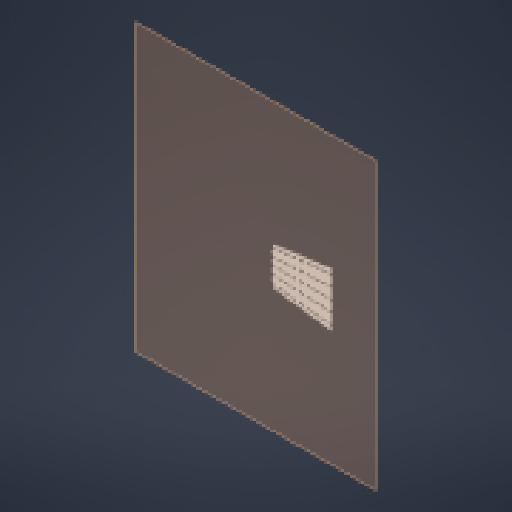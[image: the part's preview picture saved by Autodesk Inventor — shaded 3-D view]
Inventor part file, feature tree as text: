
AUTODESK INVENTOR PART (.ipt)
format: ipt  version: 2023 (Build 270158000, 158)  size: 699,904 bytes
history: native  units: in
note: dims shown in document units (in); Inventor stores cm internally (conversion verified against a paired STEP export)
features: extrude x3, sketch x3, plane x1
ambient origin geometry x8: Origin, YZ Plane, XZ Plane, XY Plane, X Axis, Y Axis, Z Axis, Center Point
bodies: Solid1 (feature_tree)
feature tree (7):
  plane  "Work Plane1"
  extrude  "Extrusion1"  TaperAngle=0.0deg  [1 undecoded]
  extrude  "Extrusion2"  Depth=0.25in
  extrude  "Extrusion3"  Depth=0.25in
  sketch  "Sketch1"  dims[d0=0.063in d1=0.0in d2=0.0in d3=0.0in]
  sketch  "Sketch2"  dims[d8=0.5in d9=0.25in]
  sketch  "Sketch3"  dims[d10=0.5in d11=0.25in d12=0.5in d13=0.25in d14=0.5in d15=0.25in d16=0.063in d17=0.0in d18=0.25in d19=0.5in d20=0.25in d21=0.5in d22=0.25in d23=0.5in d24=0.25in d25=0.5in d26=0.25in d27=0.75in d28=0.25in d29=0.75in d30=0.25in d31=0.75in d32=0.25in d33=0.75in d34=0.35in d35=0.35in d36=0.35in d37=0.35in d38=0.35in d39=0.35in d40=0.35in d41=0.35in]
note: 1 required parameter value undecoded (feature->parameter linkage not recoverable at this tier; creation-order binding heuristic only, values carry confidence <= 0.55)
